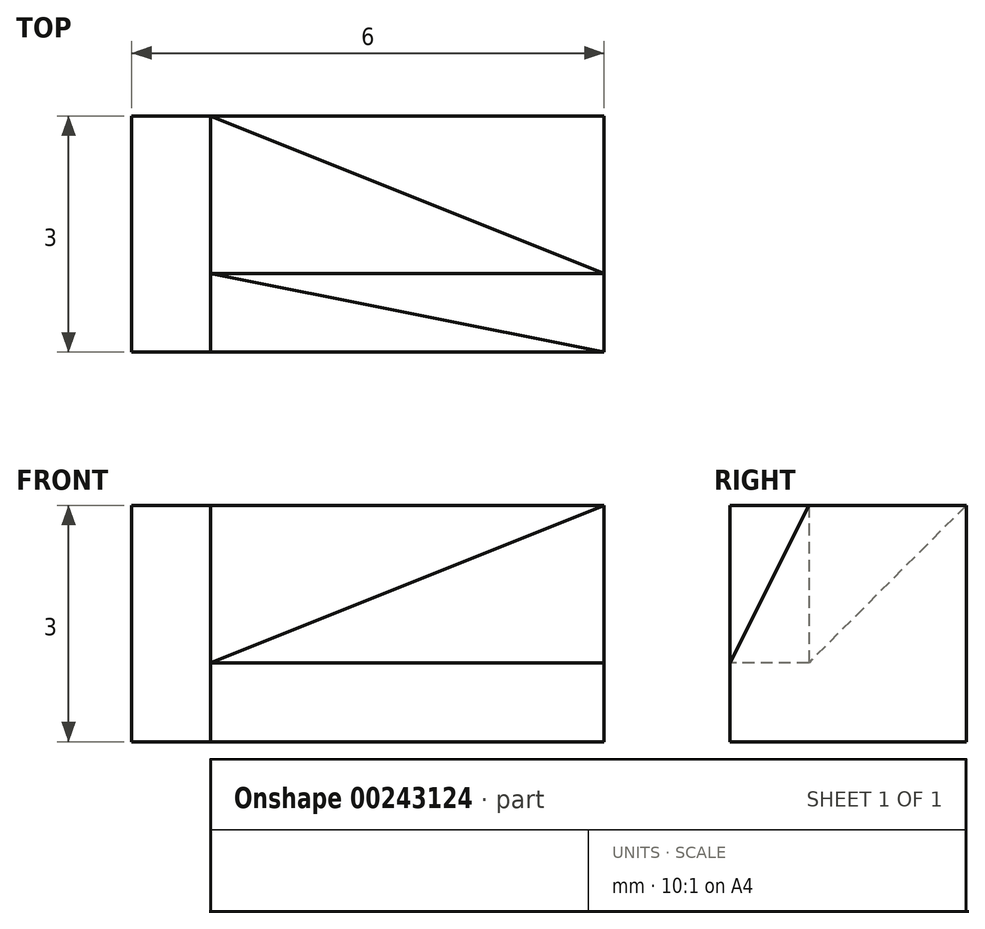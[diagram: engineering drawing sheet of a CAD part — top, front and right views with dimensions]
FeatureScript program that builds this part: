
annotation { "Feature Type Name" : "Feature", "Feature Type Description" : "" }
export const myFeature = defineFeature(function(context is Context, id is Id, definition is map)
    precondition{}
    {
        {
            var Q0;
            Q0=qCreatedBy(makeId("Top.planeOp"),FACE);
            var sketch = newSketch(context, id + "F0", { "sketchPlane" : qUnion([Q0])});
            skLineSegment(sketch, "E0", {"start": v(0, 0) * mm, "end": v(5, 0) * mm});
            skLineSegment(sketch, "E1", {"start": v(5, 0) * mm, "end": v(5, 3) * mm});
            skLineSegment(sketch, "E2", {"start": v(5, 3) * mm, "end": v(0, 3) * mm});
            skLineSegment(sketch, "E3", {"start": v(0, 3) * mm, "end": v(0, 0) * mm});
            skSolve(sketch);
        }
        {
            var Q0;
            Q0 = qSketchRegion(id + "F0", true);
            extrude(context, id + "F1", {"entities" : qUnion([Q0]), "depth" : 3 * mm});
        }
        {
            var Q0;
            Q0=makeQuery(id+"F1.opExtrude","CAP_FACE",FACE,{"disambiguationData":[OSD([sQuery(id+"F0.wireOp",EDGE,"E0"),sQuery(id+"F0.wireOp",EDGE,"E1"),sQuery(id+"F0.wireOp",EDGE,"E2"),sQuery(id+"F0.wireOp",EDGE,"E3")])],"isStart":false});
            var sketch = newSketch(context, id + "F2", { "sketchPlane" : qUnion([Q0])});
            skLineSegment(sketch, "E4", {"start": v(0, 0) * mm, "end": v(0, 1) * mm});
            skLineSegment(sketch, "E5", {"start": v(0, 1) * mm, "end": v(5, 0) * mm});
            skSolve(sketch);
        }
        {
            var Q0;
            Q0=makeQuery(id+"F2.imprint","IMPRINT",FACE,{"disambiguationData":[TD([[makeQuery(id+"F2.imprint","IMPRINT",EDGE,{"derivedFrom":sQuery(id+"F2.wireOp",EDGE,"E4")}),1.0]])]});
            extrude(context, id + "F3", {"entities" : qUnion([Q0]), "operationType" : NewBodyOperationType.REMOVE, "oppositeDirection" : true, "depth" : 2 * mm});
        }
        {
            var Q0;
            Q0=makeQuery(id+"F1.opExtrude","SWEPT_FACE",FACE,{"disambiguationData":[OSD([sQuery(id+"F0.wireOp",EDGE,"E1")])]});
            var sketch = newSketch(context, id + "F4", { "sketchPlane" : qUnion([Q0])});
            skLineSegment(sketch, "E6", {"start": v(0, 0) * mm, "end": v(1, 0) * mm});
            skLineSegment(sketch, "E7", {"start": v(1, 0) * mm, "end": v(1, 3) * mm});
            skSolve(sketch);
        }
        {
            var Q0;
            Q0=sQuery(id+"F4.wireOp",VERTEX,"E7.end");
            var Q1;
            Q1=makeQuery(id+"F3.boolean.opBoolean","COPY",VERTEX,{"derivedFrom":makeQuery(id+"F3.opExtrude","CAP_VERTEX",VERTEX,{"disambiguationData":[OSD([sQuery(id+"F0.wireOp",EDGE,"E0"),sQuery(id+"F0.wireOp",EDGE,"E1"),sQuery(id+"F2.wireOp",EDGE,"E5")])],"isStart":false})});
            var Q2;
            Q2=makeQuery(id+"F3.boolean.opBoolean","COPY",VERTEX,{"derivedFrom":makeQuery(id+"F3.opExtrude","CAP_VERTEX",VERTEX,{"disambiguationData":[OSD([sQuery(id+"F0.wireOp",EDGE,"E3"),sQuery(id+"F2.wireOp",EDGE,"E4"),sQuery(id+"F2.wireOp",EDGE,"E5")])],"isStart":false})});
            cPlane(context, id + "F5", {"entities" : qUnion([Q0, Q1, Q2]), "cplaneType" : CPlaneType.THREE_POINT, "offset" : 25 * mm, "width" : 150 * mm, "height" : 150 * mm});
        }
        {
            var Q0;
            Q0=qCreatedBy(id+"F5.planeOp",FACE);
            var sketch = newSketch(context, id + "F6", { "sketchPlane" : qUnion([Q0])});
            skPoint(sketch, "E8.0", {"position": v(-0.08, 1.34) * mm});
            skPoint(sketch, "E9.0", {"position": v(5, 3.13) * mm});
            skPoint(sketch, "E10.0", {"position": v(5, 0.9) * mm});
            skLineSegment(sketch, "E11", {"start": v(-0.08, 1.34) * mm, "end": v(5, 0.9) * mm});
            skLineSegment(sketch, "E12", {"start": v(5, 3.13) * mm, "end": v(5, 0.9) * mm});
            skLineSegment(sketch, "E13", {"start": v(5, 3.13) * mm, "end": v(-0.08, 1.34) * mm});
            skLineSegment(sketch, "E14", {"start": v(5, 3.13) * mm, "end": v(6.74, 3.13) * mm});
            skLineSegment(sketch, "E15", {"start": v(6.74, 3.13) * mm, "end": v(6.74, 0.9) * mm});
            skLineSegment(sketch, "E16", {"start": v(6.74, 0.9) * mm, "end": v(5, 0.9) * mm});
            skSolve(sketch);
        }
        {
            var Q0;
            Q0 = qSketchRegion(id + "F6", true);
            extrude(context, id + "F7", {"entities" : qUnion([Q0]), "operationType" : NewBodyOperationType.REMOVE, "depth" : 25 * mm});
        }
        {
            var Q0;
            Q0=makeQuery(id+"F1.opExtrude","CAP_VERTEX",VERTEX,{"disambiguationData":[OSD([sQuery(id+"F0.wireOp",EDGE,"E2"),sQuery(id+"F0.wireOp",EDGE,"E3")])],"isStart":false});
            var Q1;
            Q1=makeQuery(id+"F7.boolean.opBoolean","MERGE",VERTEX,{"derivedFrom":[makeQuery(id+"F3.boolean.opBoolean","COPY",VERTEX,{"derivedFrom":makeQuery(id+"F3.opExtrude","CAP_VERTEX",VERTEX,{"disambiguationData":[OSD([sQuery(id+"F0.wireOp",EDGE,"E3"),sQuery(id+"F2.wireOp",EDGE,"E4"),sQuery(id+"F2.wireOp",EDGE,"E5")])],"isStart":false})}),makeQuery(id+"F7.opExtrude","CAP_VERTEX",VERTEX,{"disambiguationData":[OSD([sQuery(id+"F6.wireOp",EDGE,"E11"),sQuery(id+"F6.wireOp",EDGE,"E13")])],"isStart":true})]});
            var Q2;
            Q2=sQuery(id+"F4.wireOp",VERTEX,"E7.end");
            cPlane(context, id + "F8", {"entities" : qUnion([Q0, Q1, Q2]), "cplaneType" : CPlaneType.THREE_POINT, "offset" : 25 * mm, "width" : 150 * mm, "height" : 150 * mm});
        }
        {
            var Q0;
            Q0=qCreatedBy(id+"F8.planeOp",FACE);
            var sketch = newSketch(context, id + "F9", { "sketchPlane" : qUnion([Q0])});
            skPoint(sketch, "E17.0", {"position": v(0, 4.24) * mm});
            skPoint(sketch, "E17.1", {"position": v(0, 1.41) * mm});
            skPoint(sketch, "E17.2", {"position": v(-5.2, 2.83) * mm});
            skLineSegment(sketch, "E18", {"start": v(0, 4.24) * mm, "end": v(0, 1.41) * mm});
            skLineSegment(sketch, "E19", {"start": v(-5.2, 2.83) * mm, "end": v(0, 4.24) * mm});
            skLineSegment(sketch, "E20", {"start": v(-5.2, 2.83) * mm, "end": v(0, 1.41) * mm});
            skLineSegment(sketch, "E21", {"start": v(-5.2, 2.83) * mm, "end": v(-5.2, 1.5) * mm});
            skLineSegment(sketch, "E22", {"start": v(-5.2, 1.5) * mm, "end": v(0, 1.41) * mm});
            skSolve(sketch);
        }
        {
            var Q0;
            Q0 = qSketchRegion(id + "F9", true);
            extrude(context, id + "F10", {"entities" : qUnion([Q0]), "operationType" : NewBodyOperationType.REMOVE, "oppositeDirection" : true, "depth" : 25 * mm});
        }
        {
            var Q0;
            Q0=qCreatedBy(makeId("Front.planeOp"),FACE);
            var sketch = newSketch(context, id + "F11", { "sketchPlane" : qUnion([Q0])});
            skLineSegment(sketch, "E23", {"start": v(0, 0) * mm, "end": v(-1, 0) * mm});
            skLineSegment(sketch, "E24", {"start": v(-1, 0) * mm, "end": v(-1, 3) * mm});
            skLineSegment(sketch, "E25", {"start": v(-1, 3) * mm, "end": v(0, 3) * mm});
            skLineSegment(sketch, "E26", {"start": v(0, 3) * mm, "end": v(0, 0) * mm});
            skSolve(sketch);
        }
        {
            var Q0;
            Q0 = qSketchRegion(id + "F11", true);
            extrude(context, id + "F12", {"entities" : qUnion([Q0]), "oppositeDirection" : true, "depth" : 3 * mm});
        }
    });
